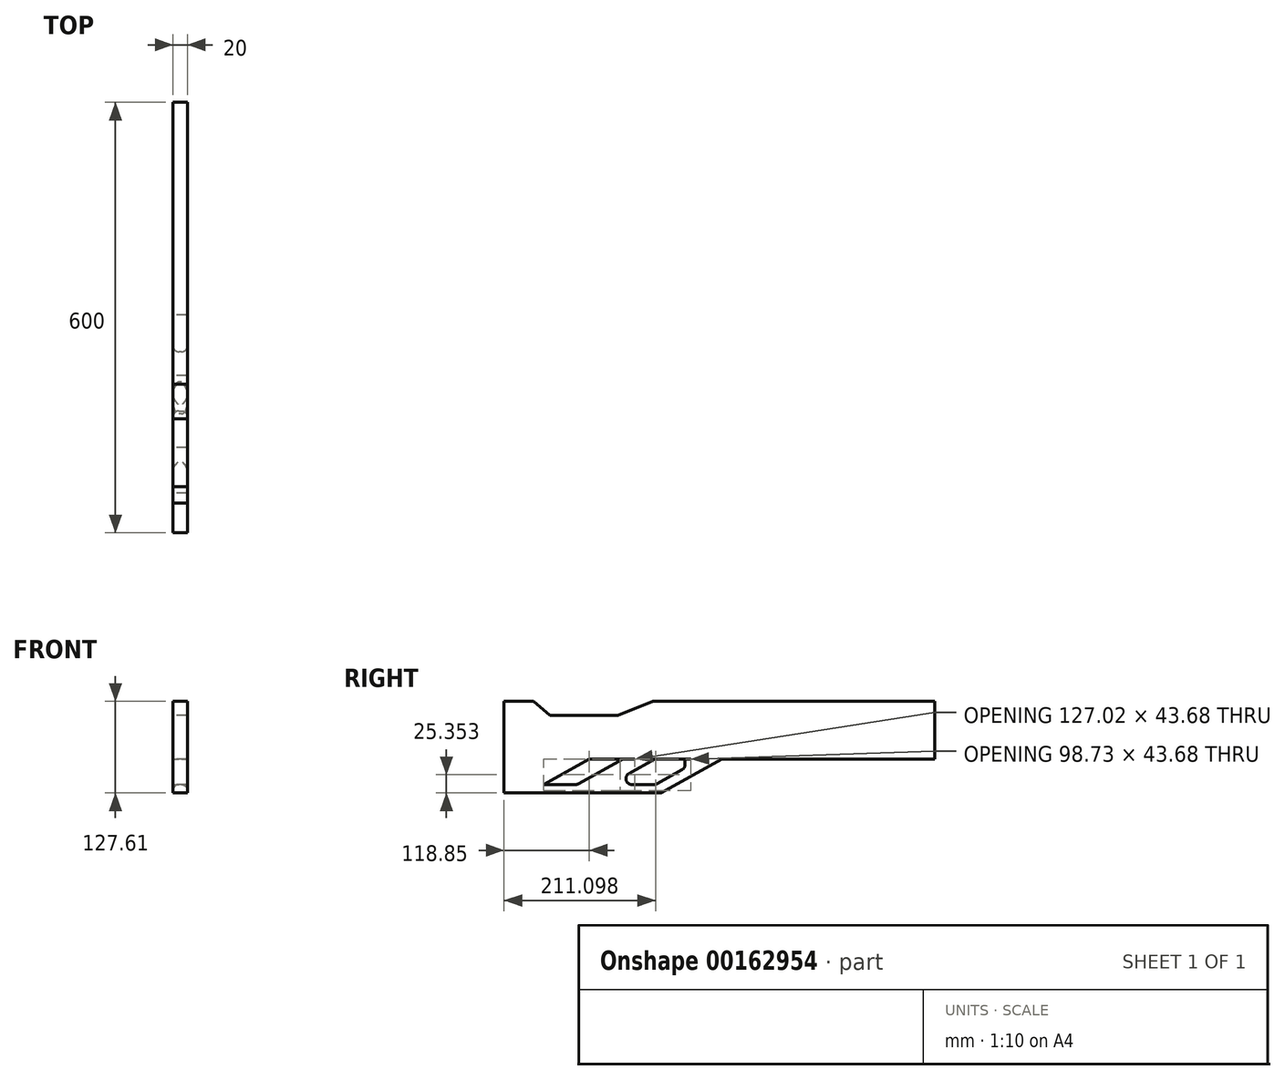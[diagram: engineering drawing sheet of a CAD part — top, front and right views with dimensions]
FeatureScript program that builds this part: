
annotation { "Feature Type Name" : "Feature", "Feature Type Description" : "" }
export const myFeature = defineFeature(function(context is Context, id is Id, definition is map)
    precondition{}
    {
        {
            var Q0;
            Q0=qCreatedBy(makeId("Right.planeOp"),FACE);
            var sketch = newSketch(context, id + "F0", { "sketchPlane" : qUnion([Q0])});
            skLineSegment(sketch, "E0.bottom", {"start": v(-296.5, 127.61) * mm, "end": v(303.5, 127.61) * mm});
            skLineSegment(sketch, "E0.top", {"start": v(-296.5, 0) * mm, "end": v(303.5, 0) * mm});
            skLineSegment(sketch, "E0.left", {"start": v(-296.5, 127.61) * mm, "end": v(-296.5, 0) * mm});
            skLineSegment(sketch, "E0.right", {"start": v(303.5, 127.61) * mm, "end": v(303.5, 0) * mm});
            skLineSegment(sketch, "E1", {"start": v(-262.04, 0) * mm, "end": v(-177.63, 47.2) * mm});
            skLineSegment(sketch, "E2", {"start": v(-177.63, 47.2) * mm, "end": v(303.5, 47.2) * mm});
            skLineSegment(sketch, "E3", {"start": v(-255.13, 127.61) * mm, "end": v(-232.35, 107.9) * mm});
            skLineSegment(sketch, "E4", {"start": v(-232.35, 107.9) * mm, "end": v(-137.56, 107.9) * mm});
            skLineSegment(sketch, "E5", {"start": v(-137.56, 107.9) * mm, "end": v(-89.14, 127.61) * mm});
            skLineSegment(sketch, "E6", {"start": v(-77.42, 0) * mm, "end": v(7, 47.2) * mm});
            skLineSegment(sketch, "E7", {"start": v(-241.15, 11.68) * mm, "end": v(-85.1, 11.68) * mm});
            skLineSegment(sketch, "E8", {"start": v(-85.1, 11.68) * mm, "end": v(-44.23, 34.52) * mm});
            skLineSegment(sketch, "E9", {"start": v(-44.23, 34.52) * mm, "end": v(-44.23, 47.2) * mm});
            skLineSegment(sketch, "E10", {"start": v(-130.95, 47.2) * mm, "end": v(-194.48, 11.68) * mm});
            skLineSegment(sketch, "E11", {"start": v(-86.48, 47.2) * mm, "end": v(-150, 11.68) * mm});
            skSolve(sketch);
        }
        {
            var Q0;
            {var subQ12=sQuery(id+"F0.wireOp",EDGE,"E0.left");Q0=makeQuery(id+"F0.imprint","IMPRINT",FACE,{"disambiguationData":[TD([[makeQuery(id+"F0.imprint","IMPRINT",EDGE,{"derivedFrom":subQ12}),1.0]])]});}
            var Q1;
            {var subQ0=sQuery(id+"F0.wireOp",EDGE,"E6");Q1=makeQuery(id+"F0.imprint","IMPRINT",FACE,{"disambiguationData":[TD([[makeQuery(id+"F0.imprint","IMPRINT",EDGE,{"derivedFrom":subQ0}),1.0]])]});}
            var Q2;
            {var subQ0=sQuery(id+"F0.wireOp",EDGE,"E10");Q2=makeQuery(id+"F0.imprint","IMPRINT",FACE,{"disambiguationData":[TD([[makeQuery(id+"F0.imprint","IMPRINT",EDGE,{"derivedFrom":subQ0}),1.0]])]});}
            extrude(context, id + "F1", {"entities" : qUnion([Q0, Q1, Q2]), "endBound" : BoundingType.SYMMETRIC, "depth" : 20 * mm, "offsetDistance" : 25 * mm});
        }
        {
            var Q0;
            Q0=makeQuery(id+"F1.opExtrude","CAP_EDGE",EDGE,{"disambiguationData":[OSD([sQuery(id+"F0.wireOp",EDGE,"E10")])],"isStart":false});
            var Q1;
            Q1=makeQuery(id+"F1.opExtrude","CAP_EDGE",EDGE,{"disambiguationData":[OSD([sQuery(id+"F0.wireOp",EDGE,"E10")])],"isStart":true});
            var Q2;
            Q2=makeQuery(id+"F1.opExtrude","CAP_EDGE",EDGE,{"disambiguationData":[OSD([sQuery(id+"F0.wireOp",EDGE,"E11")])],"isStart":true});
            var Q3;
            Q3=makeQuery(id+"F1.opExtrude","CAP_EDGE",EDGE,{"disambiguationData":[OSD([sQuery(id+"F0.wireOp",EDGE,"E11")])],"isStart":false});
            var Q4;
            Q4=makeQuery(id+"F1.opExtrude","SWEPT_EDGE",EDGE,{"disambiguationData":[OSD([sQuery(id+"F0.wireOp",EDGE,"E7"),sQuery(id+"F0.wireOp",EDGE,"E11")])]});
            var Q5;
            Q5=makeQuery(id+"F1.opExtrude","SWEPT_EDGE",EDGE,{"disambiguationData":[OSD([sQuery(id+"F0.wireOp",EDGE,"E7"),sQuery(id+"F0.wireOp",EDGE,"E10")])]});
            var Q6;
            Q6=makeQuery(id+"F1.opExtrude","CAP_EDGE",EDGE,{"disambiguationData":[OSD([sQuery(id+"F0.wireOp",EDGE,"E8")])],"isStart":true});
            var Q7;
            Q7=makeQuery(id+"F1.opExtrude","CAP_EDGE",EDGE,{"disambiguationData":[OSD([sQuery(id+"F0.wireOp",EDGE,"E9")])],"isStart":true});
            var Q8;
            Q8=makeQuery(id+"F1.opExtrude","CAP_EDGE",EDGE,{"disambiguationData":[OSD([sQuery(id+"F0.wireOp",EDGE,"E8")])],"isStart":false});
            var Q9;
            Q9=makeQuery(id+"F1.opExtrude","CAP_EDGE",EDGE,{"disambiguationData":[OSD([sQuery(id+"F0.wireOp",EDGE,"E9")])],"isStart":false});
            var Q10;
            Q10=makeQuery(id+"F1.opExtrude","SWEPT_EDGE",EDGE,{"disambiguationData":[OSD([sQuery(id+"F0.wireOp",EDGE,"E7"),sQuery(id+"F0.wireOp",EDGE,"E8")])]});
            var Q11;
            Q11=makeQuery(id+"F1.opExtrude","SWEPT_EDGE",EDGE,{"disambiguationData":[OSD([sQuery(id+"F0.wireOp",EDGE,"E8"),sQuery(id+"F0.wireOp",EDGE,"E9")])]});
            fillet(context, id + "F2", {"entities" : qUnion([Q0, Q1, Q2, Q3, Q4, Q5, Q6, Q7, Q8, Q9, Q10, Q11]), "radius" : 8.2 * mm, "tangentPropagation" : true, "allowEdgeOverflow" : false});
        }
    });
